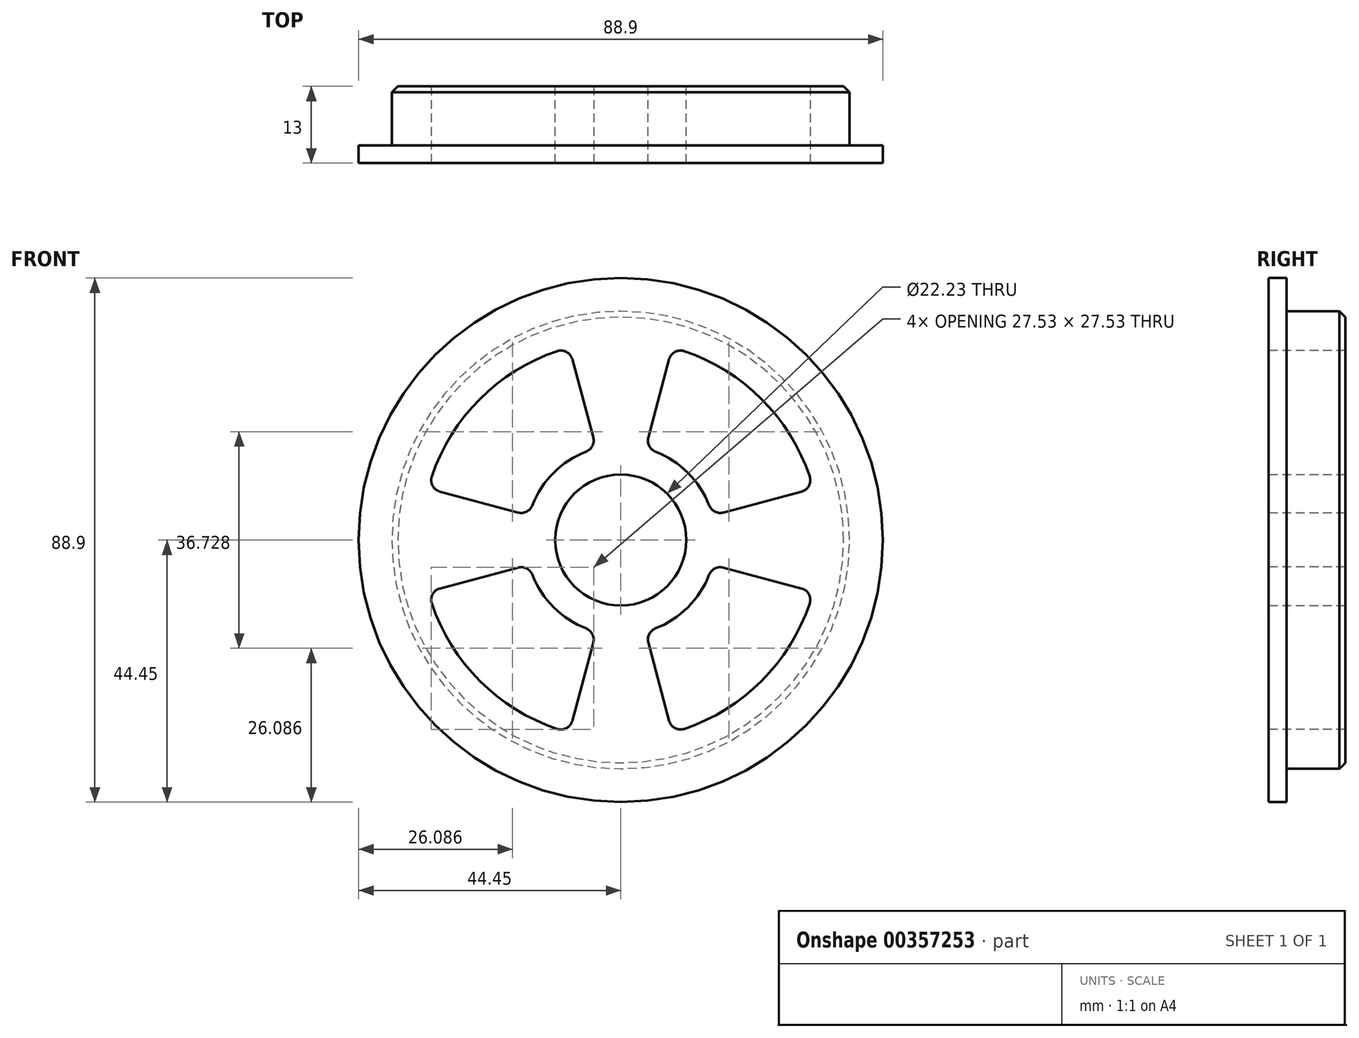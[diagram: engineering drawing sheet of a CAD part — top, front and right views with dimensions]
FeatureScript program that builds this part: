
annotation { "Feature Type Name" : "Feature", "Feature Type Description" : "" }
export const myFeature = defineFeature(function(context is Context, id is Id, definition is map)
    precondition{}
    {
        {
            var Q0;
            Q0=qCreatedBy(makeId("Front.planeOp"),FACE);
            var sketch = newSketch(context, id + "F0", { "sketchPlane" : qUnion([Q0])});
            skCircle(sketch, "E0", {"center": v(0, 0) * mm, "radius": 38.8 * mm});
            skCircle(sketch, "E1", {"center": v(0, 0) * mm, "radius": 11.11 * mm});
            skSolve(sketch);
        }
        {
            var Q0;
            Q0=makeQuery(id+"F0.imprint","IMPRINT",FACE,{"disambiguationData":[TD([[makeQuery(id+"F0.imprint","IMPRINT",EDGE,{"derivedFrom":sQuery(id+"F0.wireOp",EDGE,"E0")}),1.0]])]});
            extrude(context, id + "F1", {"entities" : qUnion([Q0]), "depth" : 12 * mm});
        }
        {
            var Q0;
            Q0=makeQuery(id+"F1.opExtrude","CAP_FACE",FACE,{"disambiguationData":[OSD([sQuery(id+"F0.wireOp",EDGE,"E0"),sQuery(id+"F0.wireOp",EDGE,"E1")])],"isStart":false});
            var sketch = newSketch(context, id + "F2", { "sketchPlane" : qUnion([Q0])});
            skCircle(sketch, "E2", {"center": v(0, 0) * mm, "radius": 44.45 * mm});
            skCircle(sketch, "E3", {"center": v(0, 0) * mm, "radius": 38.8 * mm});
            skSolve(sketch);
        }
        {
            var Q0;
            Q0=makeQuery(id+"F2.imprint","IMPRINT",FACE,{"disambiguationData":[TD([[makeQuery(id+"F2.imprint","IMPRINT",EDGE,{"derivedFrom":sQuery(id+"F2.wireOp",EDGE,"E2")}),1.0]])]});
            extrude(context, id + "F3", {"entities" : qUnion([Q0]), "operationType" : NewBodyOperationType.ADD, "oppositeDirection" : true, "depth" : 2 * mm});
        }
        {
            var Q0;
            {var subQ0=sQuery(id+"F2.wireOp",EDGE,"E3");var subQ1=sQuery(id+"F2.wireOp",EDGE,"E2");Q0=makeQuery(id+"F3.boolean.opBoolean","MERGE",FACE,{"derivedFrom":[makeQuery(id+"F1.opExtrude","CAP_FACE",FACE,{"disambiguationData":[OSD([sQuery(id+"F0.wireOp",EDGE,"E0"),sQuery(id+"F0.wireOp",EDGE,"E1")])],"isStart":false}),makeQuery(id+"F3.opExtrude","CAP_FACE",FACE,{"disambiguationData":[OSD([subQ1,subQ0,sQuery(id+"F2.wireOp",EDGE,"b3c51a6e-ffb6-4667-8beb-cc353609ae70.1.0"),sQuery(id+"F2.wireOp",EDGE,"b3c51a6e-ffb6-4667-8beb-cc353609ae70.1.1")])],"isStart":true}),makeQuery(id+"F3.opExtrude","CAP_FACE",FACE,{"disambiguationData":[OSD([subQ1,subQ0,sQuery(id+"F2.wireOp",EDGE,"b3c51a6e-ffb6-4667-8beb-cc353609ae70.2.0"),sQuery(id+"F2.wireOp",EDGE,"b3c51a6e-ffb6-4667-8beb-cc353609ae70.2.1")])],"isStart":true}),makeQuery(id+"F3.opExtrude","CAP_FACE",FACE,{"disambiguationData":[OSD([subQ1,subQ0,sQuery(id+"F2.wireOp",EDGE,"lcWJhh8i-w1F7-pef6-FBlK-XrYXNX2VGmFS"),sQuery(id+"F2.wireOp",EDGE,"48ba5e3f-722e-472f-bbf6-80e1701c8dfc0.MirrorCS")])],"isStart":true})]});}
            var sketch = newSketch(context, id + "F4", { "sketchPlane" : qUnion([Q0])});
            skCircle(sketch, "E4", {"center": v(0, 0) * mm, "radius": 9.61 * mm});
            skCircle(sketch, "E5", {"center": v(0, 0) * mm, "radius": 11.11 * mm});
            skSolve(sketch);
        }
        {
            var Q0;
            {var subQ0=sQuery(id+"F2.wireOp",EDGE,"E3");var subQ1=sQuery(id+"F2.wireOp",EDGE,"E2");Q0=makeQuery(id+"F3.boolean.opBoolean","MERGE",FACE,{"derivedFrom":[makeQuery(id+"F1.opExtrude","CAP_FACE",FACE,{"disambiguationData":[OSD([sQuery(id+"F0.wireOp",EDGE,"E0"),sQuery(id+"F0.wireOp",EDGE,"E1")])],"isStart":false}),makeQuery(id+"F3.opExtrude","CAP_FACE",FACE,{"disambiguationData":[OSD([subQ1,subQ0,sQuery(id+"F2.wireOp",EDGE,"27980060-e5c7-4240-b4d6-3186c7cb0f6e.2.0"),sQuery(id+"F2.wireOp",EDGE,"27980060-e5c7-4240-b4d6-3186c7cb0f6e.2.1")])],"isStart":true}),makeQuery(id+"F3.opExtrude","CAP_FACE",FACE,{"disambiguationData":[OSD([subQ1,subQ0,sQuery(id+"F2.wireOp",EDGE,"27980060-e5c7-4240-b4d6-3186c7cb0f6e.1.0"),sQuery(id+"F2.wireOp",EDGE,"27980060-e5c7-4240-b4d6-3186c7cb0f6e.1.1")])],"isStart":true}),makeQuery(id+"F3.opExtrude","CAP_FACE",FACE,{"disambiguationData":[OSD([subQ1,subQ0,sQuery(id+"F2.wireOp",EDGE,"lcWJhh8i-w1F7-pef6-FBlK-XrYXNX2VGmFS"),sQuery(id+"F2.wireOp",EDGE,"48ba5e3f-722e-472f-bbf6-80e1701c8dfc0.MirrorCS")])],"isStart":true}),makeQuery(id+"F3.opExtrude","CAP_FACE",FACE,{"disambiguationData":[OSD([subQ1,subQ0,sQuery(id+"F2.wireOp",EDGE,"27980060-e5c7-4240-b4d6-3186c7cb0f6e.3.0"),sQuery(id+"F2.wireOp",EDGE,"27980060-e5c7-4240-b4d6-3186c7cb0f6e.3.1")])],"isStart":true})]});}
            var sketch = newSketch(context, id + "F5", { "sketchPlane" : qUnion([Q0])});
            skLineSegment(sketch, "E6", {"start": v(0, 0) * mm, "end": v(0, -44.45) * mm, "construction": true});
            skCircle(sketch, "E7", {"center": v(0, 0) * mm, "radius": 33.8 * mm});
            skLineSegment(sketch, "E8", {"start": v(0, 0) * mm, "end": v(8.75, -32.65) * mm});
            skLineSegment(sketch, "E9.MirrorCS", {"start": v(0, 0) * mm, "end": v(-8.75, -32.65) * mm});
            skLineSegment(sketch, "E10.1.0", {"start": v(0, 0) * mm, "end": v(32.65, 8.75) * mm});
            skLineSegment(sketch, "E10.1.1", {"start": v(0, 0) * mm, "end": v(32.65, -8.75) * mm});
            skLineSegment(sketch, "E10.2.0", {"start": v(0, 0) * mm, "end": v(-8.75, 32.65) * mm});
            skLineSegment(sketch, "E10.2.1", {"start": v(0, 0) * mm, "end": v(8.75, 32.65) * mm});
            skLineSegment(sketch, "E10.3.0", {"start": v(0, 0) * mm, "end": v(-32.65, -8.75) * mm});
            skLineSegment(sketch, "E10.3.1", {"start": v(0, 0) * mm, "end": v(-32.65, 8.75) * mm});
            skCircle(sketch, "E11", {"center": v(0, 0) * mm, "radius": 16.11 * mm});
            skSolve(sketch);
        }
        {
            var Q0;
            {var subQ0=sQuery(id+"F5.wireOp",EDGE,"E8");var subQ1=sQuery(id+"F5.wireOp",EDGE,"E7");var subQ2=makeQuery(id+"F5.imprint","INTERSECT",VERTEX,{"derivedFrom":[subQ1,subQ0]});Q0=makeQuery(id+"F5.imprint","IMPRINT",FACE,{"disambiguationData":[TD([[makeQuery(id+"F5.imprint","IMPRINT",EDGE,{"disambiguationData":[TD([[subQ2,-1.0]])],"derivedFrom":subQ1}),1.0]])]});}
            var Q1;
            {var subQ0=sQuery(id+"F5.wireOp",EDGE,"E9.MirrorCS");var subQ1=sQuery(id+"F5.wireOp",EDGE,"E7");var subQ2=makeQuery(id+"F5.imprint","INTERSECT",VERTEX,{"derivedFrom":[subQ1,subQ0]});Q1=makeQuery(id+"F5.imprint","IMPRINT",FACE,{"disambiguationData":[TD([[makeQuery(id+"F5.imprint","IMPRINT",EDGE,{"disambiguationData":[TD([[subQ2,1.0]])],"derivedFrom":subQ1}),1.0]])]});}
            var Q2;
            {var subQ0=sQuery(id+"F5.wireOp",EDGE,"E10.2.0");var subQ1=sQuery(id+"F5.wireOp",EDGE,"E7");var subQ2=makeQuery(id+"F5.imprint","INTERSECT",VERTEX,{"derivedFrom":[subQ1,subQ0]});Q2=makeQuery(id+"F5.imprint","IMPRINT",FACE,{"disambiguationData":[TD([[makeQuery(id+"F5.imprint","IMPRINT",EDGE,{"disambiguationData":[TD([[subQ2,-1.0]])],"derivedFrom":subQ1}),1.0]])]});}
            var Q3;
            {var subQ0=sQuery(id+"F5.wireOp",EDGE,"E10.1.0");var subQ1=sQuery(id+"F5.wireOp",EDGE,"E7");var subQ2=makeQuery(id+"F5.imprint","INTERSECT",VERTEX,{"derivedFrom":[subQ1,subQ0]});Q3=makeQuery(id+"F5.imprint","IMPRINT",FACE,{"disambiguationData":[TD([[makeQuery(id+"F5.imprint","IMPRINT",EDGE,{"disambiguationData":[TD([[subQ2,-1.0]])],"derivedFrom":subQ1}),1.0]])]});}
            extrude(context, id + "F6", {"entities" : qUnion([Q0, Q1, Q2, Q3]), "operationType" : NewBodyOperationType.REMOVE, "oppositeDirection" : true, "depth" : 25 * mm});
        }
        {
            var Q0;
            Q0=makeQuery(id+"F6.boolean.opBoolean","COPY",EDGE,{"derivedFrom":makeQuery(id+"F6.opExtrude","SWEPT_EDGE",EDGE,{"disambiguationData":[OSD([sQuery(id+"F5.wireOp",EDGE,"E7"),sQuery(id+"F5.wireOp",EDGE,"E9.MirrorCS")])]})});
            var Q1;
            Q1=makeQuery(id+"F6.boolean.opBoolean","COPY",EDGE,{"derivedFrom":makeQuery(id+"F6.opExtrude","SWEPT_EDGE",EDGE,{"disambiguationData":[OSD([sQuery(id+"F5.wireOp",EDGE,"E9.MirrorCS"),sQuery(id+"F5.wireOp",EDGE,"E11")])]})});
            var Q2;
            Q2=makeQuery(id+"F6.boolean.opBoolean","COPY",EDGE,{"derivedFrom":makeQuery(id+"F6.opExtrude","SWEPT_EDGE",EDGE,{"disambiguationData":[OSD([sQuery(id+"F5.wireOp",EDGE,"E10.3.0"),sQuery(id+"F5.wireOp",EDGE,"E11")])]})});
            var Q3;
            Q3=makeQuery(id+"F6.boolean.opBoolean","COPY",EDGE,{"derivedFrom":makeQuery(id+"F6.opExtrude","SWEPT_EDGE",EDGE,{"disambiguationData":[OSD([sQuery(id+"F5.wireOp",EDGE,"E7"),sQuery(id+"F5.wireOp",EDGE,"E10.3.0")])]})});
            var Q4;
            Q4=makeQuery(id+"F6.boolean.opBoolean","COPY",EDGE,{"derivedFrom":makeQuery(id+"F6.opExtrude","SWEPT_EDGE",EDGE,{"disambiguationData":[OSD([sQuery(id+"F5.wireOp",EDGE,"E8"),sQuery(id+"F5.wireOp",EDGE,"E11")])]})});
            var Q5;
            Q5=makeQuery(id+"F6.boolean.opBoolean","COPY",EDGE,{"derivedFrom":makeQuery(id+"F6.opExtrude","SWEPT_EDGE",EDGE,{"disambiguationData":[OSD([sQuery(id+"F5.wireOp",EDGE,"E7"),sQuery(id+"F5.wireOp",EDGE,"E8")])]})});
            var Q6;
            Q6=makeQuery(id+"F6.boolean.opBoolean","COPY",EDGE,{"derivedFrom":makeQuery(id+"F6.opExtrude","SWEPT_EDGE",EDGE,{"disambiguationData":[OSD([sQuery(id+"F5.wireOp",EDGE,"E10.1.1"),sQuery(id+"F5.wireOp",EDGE,"E11")])]})});
            var Q7;
            Q7=makeQuery(id+"F6.boolean.opBoolean","COPY",EDGE,{"derivedFrom":makeQuery(id+"F6.opExtrude","SWEPT_EDGE",EDGE,{"disambiguationData":[OSD([sQuery(id+"F5.wireOp",EDGE,"E7"),sQuery(id+"F5.wireOp",EDGE,"E10.1.1")])]})});
            var Q8;
            Q8=makeQuery(id+"F6.boolean.opBoolean","COPY",EDGE,{"derivedFrom":makeQuery(id+"F6.opExtrude","SWEPT_EDGE",EDGE,{"disambiguationData":[OSD([sQuery(id+"F5.wireOp",EDGE,"E7"),sQuery(id+"F5.wireOp",EDGE,"E10.2.1")])]})});
            var Q9;
            Q9=makeQuery(id+"F6.boolean.opBoolean","COPY",EDGE,{"derivedFrom":makeQuery(id+"F6.opExtrude","SWEPT_EDGE",EDGE,{"disambiguationData":[OSD([sQuery(id+"F5.wireOp",EDGE,"E7"),sQuery(id+"F5.wireOp",EDGE,"E10.1.0")])]})});
            var Q10;
            Q10=makeQuery(id+"F6.boolean.opBoolean","COPY",EDGE,{"derivedFrom":makeQuery(id+"F6.opExtrude","SWEPT_EDGE",EDGE,{"disambiguationData":[OSD([sQuery(id+"F5.wireOp",EDGE,"E10.1.0"),sQuery(id+"F5.wireOp",EDGE,"E11")])]})});
            var Q11;
            Q11=makeQuery(id+"F6.boolean.opBoolean","COPY",EDGE,{"derivedFrom":makeQuery(id+"F6.opExtrude","SWEPT_EDGE",EDGE,{"disambiguationData":[OSD([sQuery(id+"F5.wireOp",EDGE,"E10.2.1"),sQuery(id+"F5.wireOp",EDGE,"E11")])]})});
            var Q12;
            Q12=makeQuery(id+"F6.boolean.opBoolean","COPY",EDGE,{"derivedFrom":makeQuery(id+"F6.opExtrude","SWEPT_EDGE",EDGE,{"disambiguationData":[OSD([sQuery(id+"F5.wireOp",EDGE,"E10.2.0"),sQuery(id+"F5.wireOp",EDGE,"E11")])]})});
            var Q13;
            Q13=makeQuery(id+"F6.boolean.opBoolean","COPY",EDGE,{"derivedFrom":makeQuery(id+"F6.opExtrude","SWEPT_EDGE",EDGE,{"disambiguationData":[OSD([sQuery(id+"F5.wireOp",EDGE,"E10.3.1"),sQuery(id+"F5.wireOp",EDGE,"E11")])]})});
            var Q14;
            Q14=makeQuery(id+"F6.boolean.opBoolean","COPY",EDGE,{"derivedFrom":makeQuery(id+"F6.opExtrude","SWEPT_EDGE",EDGE,{"disambiguationData":[OSD([sQuery(id+"F5.wireOp",EDGE,"E7"),sQuery(id+"F5.wireOp",EDGE,"E10.2.0")])]})});
            var Q15;
            Q15=makeQuery(id+"F6.boolean.opBoolean","COPY",EDGE,{"derivedFrom":makeQuery(id+"F6.opExtrude","SWEPT_EDGE",EDGE,{"disambiguationData":[OSD([sQuery(id+"F5.wireOp",EDGE,"E7"),sQuery(id+"F5.wireOp",EDGE,"E10.3.1")])]})});
            var Q16;
            Q16=makeQuery(id+"F3.opExtrude","SWEPT_EDGE",EDGE,{"disambiguationData":[OSD([sQuery(id+"F2.wireOp",EDGE,"E3"),sQuery(id+"F2.wireOp",EDGE,"27980060-e5c7-4240-b4d6-3186c7cb0f6e.3.1")])]});
            var Q17;
            Q17=makeQuery(id+"F3.opExtrude","SWEPT_EDGE",EDGE,{"disambiguationData":[OSD([sQuery(id+"F2.wireOp",EDGE,"E3"),sQuery(id+"F2.wireOp",EDGE,"lcWJhh8i-w1F7-pef6-FBlK-XrYXNX2VGmFS")])]});
            var Q18;
            Q18=makeQuery(id+"F3.opExtrude","SWEPT_EDGE",EDGE,{"disambiguationData":[OSD([sQuery(id+"F2.wireOp",EDGE,"E3"),sQuery(id+"F2.wireOp",EDGE,"48ba5e3f-722e-472f-bbf6-80e1701c8dfc0.MirrorCS")])]});
            var Q19;
            Q19=makeQuery(id+"F3.opExtrude","SWEPT_EDGE",EDGE,{"disambiguationData":[OSD([sQuery(id+"F2.wireOp",EDGE,"E3"),sQuery(id+"F2.wireOp",EDGE,"27980060-e5c7-4240-b4d6-3186c7cb0f6e.1.0")])]});
            var Q20;
            Q20=makeQuery(id+"F3.opExtrude","SWEPT_EDGE",EDGE,{"disambiguationData":[OSD([sQuery(id+"F2.wireOp",EDGE,"E3"),sQuery(id+"F2.wireOp",EDGE,"27980060-e5c7-4240-b4d6-3186c7cb0f6e.1.1")])]});
            var Q21;
            Q21=makeQuery(id+"F3.opExtrude","SWEPT_EDGE",EDGE,{"disambiguationData":[OSD([sQuery(id+"F2.wireOp",EDGE,"E3"),sQuery(id+"F2.wireOp",EDGE,"27980060-e5c7-4240-b4d6-3186c7cb0f6e.2.0")])]});
            var Q22;
            Q22=makeQuery(id+"F3.opExtrude","SWEPT_EDGE",EDGE,{"disambiguationData":[OSD([sQuery(id+"F2.wireOp",EDGE,"E3"),sQuery(id+"F2.wireOp",EDGE,"27980060-e5c7-4240-b4d6-3186c7cb0f6e.2.1")])]});
            var Q23;
            Q23=makeQuery(id+"F3.opExtrude","SWEPT_EDGE",EDGE,{"disambiguationData":[OSD([sQuery(id+"F2.wireOp",EDGE,"E3"),sQuery(id+"F2.wireOp",EDGE,"27980060-e5c7-4240-b4d6-3186c7cb0f6e.3.0")])]});
            fillet(context, id + "F7", {"entities" : qUnion([Q0, Q1, Q2, Q3, Q4, Q5, Q6, Q7, Q8, Q9, Q10, Q11, Q12, Q13, Q14, Q15, Q16, Q17, Q18, Q19, Q20, Q21, Q22, Q23]), "radius" : 2 * mm, "tangentPropagation" : true, "allowEdgeOverflow" : false});
        }
        {
            var Q0;
            Q0=makeQuery(id+"F1.opExtrude","CAP_EDGE",EDGE,{"disambiguationData":[OSD([sQuery(id+"F0.wireOp",EDGE,"E0")])],"isStart":true});
            chamfer(context, id + "F8", {"entities" : qUnion([Q0]), "width" : 1 * mm, "tangentPropagation" : true});
        }
        {
            var Q0;
            Q0=makeQuery(id+"F3.boolean.opBoolean","MERGE",FACE,{"derivedFrom":[makeQuery(id+"F1.opExtrude","CAP_FACE",FACE,{"disambiguationData":[OSD([sQuery(id+"F0.wireOp",EDGE,"E0"),sQuery(id+"F0.wireOp",EDGE,"E1")])],"isStart":false}),makeQuery(id+"F3.opExtrude","CAP_FACE",FACE,{"disambiguationData":[OSD([sQuery(id+"F2.wireOp",EDGE,"E2"),sQuery(id+"F2.wireOp",EDGE,"E3")])],"isStart":true})]});
            extrude(context, id + "F9", {"entities" : qUnion([Q0]), "operationType" : NewBodyOperationType.ADD, "depth" : 1 * mm});
        }
    });
